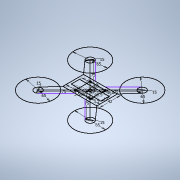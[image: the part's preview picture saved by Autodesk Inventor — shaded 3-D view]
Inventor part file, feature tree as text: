
AUTODESK INVENTOR PART (.ipt)
format: ipt  version: 2021 (Build 250183000, 183)  size: 138,752 bytes
history: native  units: in
note: dims shown in document units (in); Inventor stores cm internally (conversion verified against a paired STEP export)
features: sketch x2
ambient origin geometry x8: Origin, YZ Plane, XZ Plane, XY Plane, X Axis, Y Axis, Z Axis, Center Point
feature tree (2):
  sketch  "Sketch1"  dims[d0=1.2008in]
  sketch  "Sketch2"  dims[d1=1.2008in d2=0.1378in d3=0.1378in d4=0.1378in d5=0.1378in d6=1.6535in d7=0.1969in d8=0.1969in d9=0.1969in d10=0.1969in d11=1.7717in d14=2.3622in d15=0.6693in d16=0.1969in d17=0.1969in d20=2.9528in d21=2.9528in d22=2.9528in d23=2.5591in d24=2.5591in d25=2.5591in d26=2.5591in d27=2.9528in d28=0.5906in d29=0.5906in d31=0.5906in d32=0.5906in d33=2.7165in d34=1.6535in d35=1.2008in d36=1.2008in d37=0.1378in d38=0.1378in d39=0.1378in d40=0.1378in]
